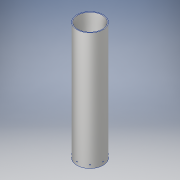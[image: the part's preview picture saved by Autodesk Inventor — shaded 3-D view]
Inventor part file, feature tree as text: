
AUTODESK INVENTOR PART (.ipt)
format: ipt  version: 2017 SP1 (Build 210196100, 196)  size: 130,560 bytes
history: native  units: in
note: dims shown in document units (in); Inventor stores cm internally (conversion verified against a paired STEP export)
features: sketch x2, extrude x1, plane x1, hole x1, pattern_circular x1
ambient origin geometry x8: Origin, YZ Plane, XZ Plane, XY Plane, X Axis, Y Axis, Z Axis, Center Point
bodies: Solid1 (feature_tree)
feature tree (6):
  extrude  "Extrusion1"  Depth=7.5in
  plane  "Work Plane1"
  hole  "Hole1"  [1 undecoded]
  pattern_circular  "Circular Pattern1"  Count=8 Angle=360.0deg
  sketch  "Sketch1"  dims[d0=8.0in d1=7.5in]
  sketch  "Sketch2"  dims[d2=36.0in d3=0.0in d4=1.0in d5=0.25in d6=0.75in d7=0.375in d8=0.25in d9=0.5635in d10=1.0in d11=0.8108in d12=3.1496in d13=360.0deg]
note: 1 required parameter value undecoded (feature->parameter linkage not recoverable at this tier; creation-order binding heuristic only, values carry confidence <= 0.55)
